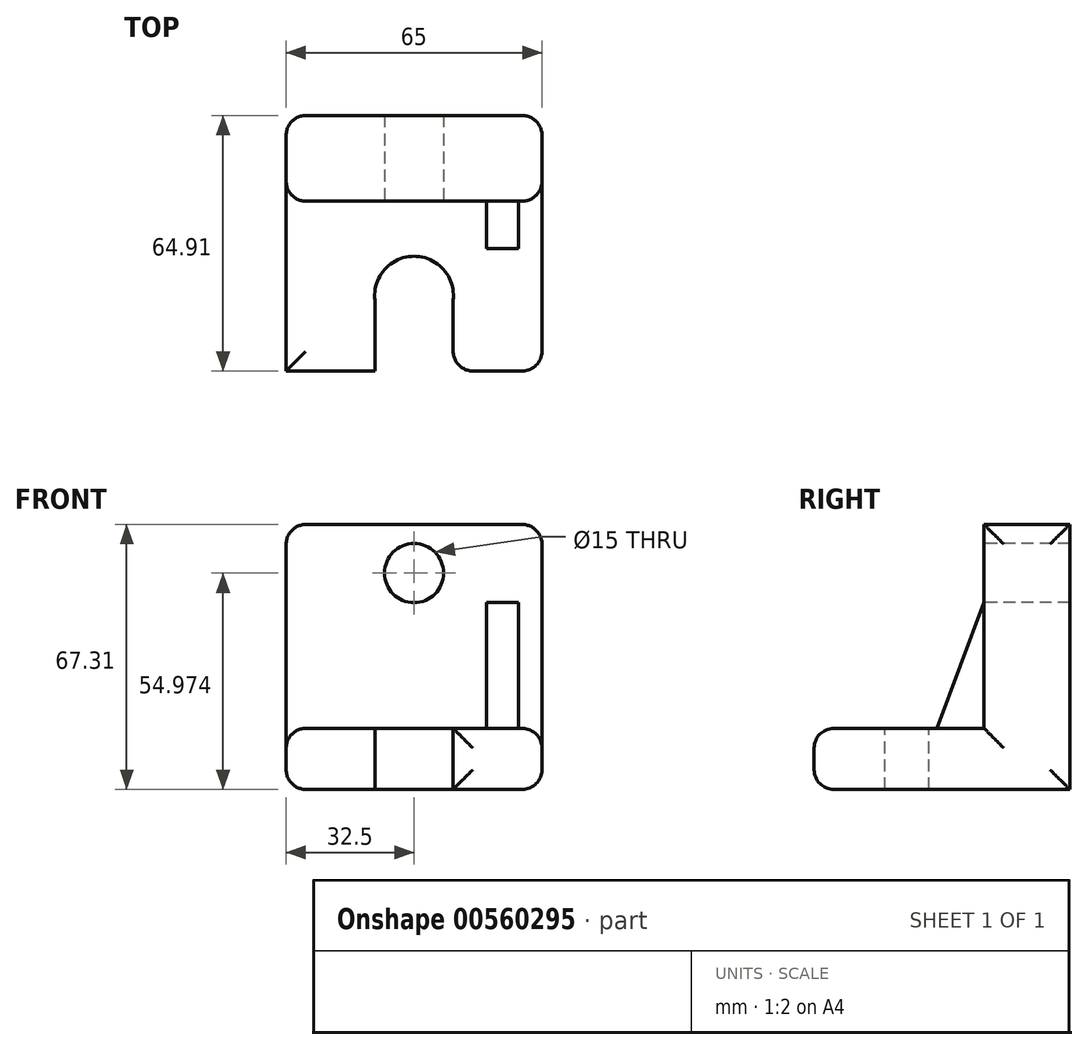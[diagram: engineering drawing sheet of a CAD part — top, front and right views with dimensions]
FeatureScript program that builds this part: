
annotation { "Feature Type Name" : "Feature", "Feature Type Description" : "" }
export const myFeature = defineFeature(function(context is Context, id is Id, definition is map)
    precondition{}
    {
        {
            var Q0;
            Q0=qCreatedBy(makeId("Right.planeOp"),FACE);
            var sketch = newSketch(context, id + "F0", { "sketchPlane" : qUnion([Q0])});
            skLineSegment(sketch, "E0", {"start": v(0, 0) * mm, "end": v(0, 67.3) * mm});
            skLineSegment(sketch, "E1", {"start": v(0, 67.3) * mm, "end": v(-21.74, 67.3) * mm});
            skLineSegment(sketch, "E2", {"start": v(-21.74, 67.3) * mm, "end": v(-21.74, 15.5) * mm});
            skLineSegment(sketch, "E3", {"start": v(-21.74, 15.5) * mm, "end": v(-64.91, 15.5) * mm});
            skLineSegment(sketch, "E4", {"start": v(-64.91, 15.5) * mm, "end": v(-64.91, 0) * mm});
            skLineSegment(sketch, "E5", {"start": v(-64.91, 0) * mm, "end": v(0, 0) * mm});
            skSolve(sketch);
        }
        {
            var Q0;
            Q0=makeQuery(id+"F0.imprint","IMPRINT",FACE,{"disambiguationData":[TD([[makeQuery(id+"F0.imprint","IMPRINT",EDGE,{"derivedFrom":sQuery(id+"F0.wireOp",EDGE,"E0")}),1.0]])]});
            extrude(context, id + "F1", {"entities" : qUnion([Q0]), "depth" : 65 * mm, "offsetDistance" : 25 * mm});
        }
        {
            var Q0;
            Q0=makeQuery(id+"F1.opExtrude","SWEPT_FACE",FACE,{"disambiguationData":[OSD([sQuery(id+"F0.wireOp",EDGE,"E2")])]});
            var sketch = newSketch(context, id + "F2", { "sketchPlane" : qUnion([Q0])});
            skCircle(sketch, "E6", {"center": v(32.5, 54.97) * mm, "radius": 7.5 * mm});
            skLineSegment(sketch, "E7", {"start": v(32.5, 67.3) * mm, "end": v(32.5, 12.95) * mm, "construction": true});
            skSolve(sketch);
        }
        {
            var Q0;
            Q0=makeQuery(id+"F2.imprint","IMPRINT",FACE,{"disambiguationData":[TD([[makeQuery(id+"F2.imprint","IMPRINT",EDGE,{"derivedFrom":sQuery(id+"F2.wireOp",EDGE,"E6")}),1.0]])]});
            extrude(context, id + "F3", {"entities" : qUnion([Q0]), "operationType" : NewBodyOperationType.REMOVE, "oppositeDirection" : true, "depth" : 25 * mm, "offsetDistance" : 25 * mm});
        }
        {
            var Q0;
            Q0=makeQuery(id+"F1.opExtrude","SWEPT_FACE",FACE,{"disambiguationData":[OSD([sQuery(id+"F0.wireOp",EDGE,"E3")])]});
            var sketch = newSketch(context, id + "F4", { "sketchPlane" : qUnion([Q0])});
            skLineSegment(sketch, "E8", {"start": v(32.5, -21.74) * mm, "end": v(32.5, -64.91) * mm, "construction": true});
            skArc(sketch, "E9", {"start": v(42.43, -46.92) * mm, "mid": v(32.5, -35.76) * mm, "end": v(22.57, -46.92) * mm});
            skLineSegment(sketch, "E10", {"start": v(22.57, -46.92) * mm, "end": v(22.57, -64.91) * mm});
            skLineSegment(sketch, "E11", {"start": v(42.43, -46.92) * mm, "end": v(42.43, -64.91) * mm});
            skSolve(sketch);
        }
        {
            var Q0;
            Q0=makeQuery(id+"F4.imprint","IMPRINT",FACE,{"disambiguationData":[TD([[makeQuery(id+"F4.imprint","IMPRINT",EDGE,{"derivedFrom":sQuery(id+"F4.wireOp",EDGE,"E9")}),1.0]])]});
            extrude(context, id + "F5", {"entities" : qUnion([Q0]), "operationType" : NewBodyOperationType.REMOVE, "endBound" : BoundingType.UP_TO_NEXT, "oppositeDirection" : true, "depth" : 10.1 * mm, "offsetDistance" : 25 * mm});
        }
        {
            var Q0;
            Q0=qCreatedBy(makeId("Right.planeOp"),FACE);
            cPlane(context, id + "F6", {"entities" : qUnion([Q0]), "cplaneType" : CPlaneType.OFFSET, "offset" : 55 * mm, "width" : 150 * mm, "height" : 150 * mm});
        }
        {
            var Q0;
            Q0=qCreatedBy(id+"F6.planeOp",FACE);
            var sketch = newSketch(context, id + "F7", { "sketchPlane" : qUnion([Q0])});
            skLineSegment(sketch, "E12.0", {"start": v(-21.74, 47.5) * mm, "end": v(-21.74, 15.5) * mm});
            skLineSegment(sketch, "E13.0", {"start": v(-21.74, 15.5) * mm, "end": v(-33.74, 15.5) * mm});
            skLineSegment(sketch, "E14.0.4", {"start": v(-21.74, 67.3) * mm, "end": v(-21.74, 15.5) * mm});
            skLineSegment(sketch, "E15", {"start": v(-21.74, 47.5) * mm, "end": v(-33.74, 15.5) * mm});
            skSolve(sketch);
        }
        {
            var Q0;
            {var subQ0=sQuery(id+"F7.wireOp",EDGE,"E13.0");Q0=makeQuery(id+"F7.imprint","IMPRINT",FACE,{"disambiguationData":[TD([[makeQuery(id+"F7.imprint","IMPRINT",EDGE,{"derivedFrom":subQ0}),-1.0]])]});}
            extrude(context, id + "F8", {"entities" : qUnion([Q0]), "operationType" : NewBodyOperationType.ADD, "endBound" : BoundingType.SYMMETRIC, "depth" : 8.2 * mm, "offsetDistance" : 25 * mm});
        }
        {
            var Q0;
            Q0=makeQuery(id+"F1.opExtrude","CAP_EDGE",EDGE,{"disambiguationData":[OSD([sQuery(id+"F0.wireOp",EDGE,"E1")])],"isStart":true});
            var Q1;
            Q1=makeQuery(id+"F1.opExtrude","CAP_EDGE",EDGE,{"disambiguationData":[OSD([sQuery(id+"F0.wireOp",EDGE,"E1")])],"isStart":false});
            var Q2;
            {var subQ0=sQuery(id+"F0.wireOp",EDGE,"E4");var subQ1=sQuery(id+"F0.wireOp",EDGE,"E3");Q2=makeQuery(id+"F5.boolean.opBoolean","SPLIT",EDGE,{"disambiguationData":[TD([makeQuery(id+"F5.opExtrude","SWEPT_FACE",FACE,{"disambiguationData":[OSD([sQuery(id+"F4.wireOp",EDGE,"E10")])]})])],"derivedFrom":makeQuery(id+"F1.opExtrude","SWEPT_EDGE",EDGE,{"disambiguationData":[OSD([subQ1,subQ0])]})});}
            var Q3;
            Q3=makeQuery(id+"F1.opExtrude","CAP_EDGE",EDGE,{"disambiguationData":[OSD([sQuery(id+"F0.wireOp",EDGE,"E3")])],"isStart":true});
            var Q4;
            Q4=makeQuery(id+"F1.opExtrude","CAP_EDGE",EDGE,{"disambiguationData":[OSD([sQuery(id+"F0.wireOp",EDGE,"E2")])],"isStart":true});
            var Q5;
            Q5=makeQuery(id+"F1.opExtrude","CAP_EDGE",EDGE,{"disambiguationData":[OSD([sQuery(id+"F0.wireOp",EDGE,"E0")])],"isStart":true});
            var Q6;
            Q6=makeQuery(id+"F1.opExtrude","CAP_EDGE",EDGE,{"disambiguationData":[OSD([sQuery(id+"F0.wireOp",EDGE,"E5")])],"isStart":true});
            var Q7;
            {var subQ0=sQuery(id+"F0.wireOp",EDGE,"E5");var subQ1=sQuery(id+"F0.wireOp",EDGE,"E4");Q7=makeQuery(id+"F5.boolean.opBoolean","SPLIT",EDGE,{"disambiguationData":[TD([makeQuery(id+"F5.opExtrude","SWEPT_FACE",FACE,{"disambiguationData":[OSD([sQuery(id+"F4.wireOp",EDGE,"E10")])]})])],"derivedFrom":makeQuery(id+"F1.opExtrude","SWEPT_EDGE",EDGE,{"disambiguationData":[OSD([subQ1,subQ0])]})});}
            var Q8;
            Q8=makeQuery(id+"F1.opExtrude","CAP_EDGE",EDGE,{"disambiguationData":[OSD([sQuery(id+"F0.wireOp",EDGE,"E4")])],"isStart":false});
            var Q9;
            Q9=makeQuery(id+"F1.opExtrude","CAP_EDGE",EDGE,{"disambiguationData":[OSD([sQuery(id+"F0.wireOp",EDGE,"E3")])],"isStart":false});
            var Q10;
            Q10=makeQuery(id+"F1.opExtrude","CAP_EDGE",EDGE,{"disambiguationData":[OSD([sQuery(id+"F0.wireOp",EDGE,"E2")])],"isStart":false});
            var Q11;
            Q11=makeQuery(id+"F1.opExtrude","CAP_EDGE",EDGE,{"disambiguationData":[OSD([sQuery(id+"F0.wireOp",EDGE,"E0")])],"isStart":false});
            var Q12;
            Q12=makeQuery(id+"F1.opExtrude","CAP_EDGE",EDGE,{"disambiguationData":[OSD([sQuery(id+"F0.wireOp",EDGE,"E5")])],"isStart":false});
            var Q13;
            {var subQ1=sQuery(id+"F0.wireOp",EDGE,"E4");Q13=makeQuery(id+"F5.boolean.opBoolean","SPLIT",FACE,{"disambiguationData":[TD([makeQuery(id+"F5.opExtrude","SWEPT_FACE",FACE,{"disambiguationData":[OSD([sQuery(id+"F4.wireOp",EDGE,"E11")])]})])],"derivedFrom":makeQuery(id+"F1.opExtrude","SWEPT_FACE",FACE,{"disambiguationData":[OSD([subQ1])]})});}
            var Q14;
            Q14=makeQuery(id+"F8.opExtrude","SWEPT_EDGE",EDGE,{"disambiguationData":[OSD([sQuery(id+"F7.wireOp",EDGE,"E13.0"),sQuery(id+"F7.wireOp",EDGE,"E15")])]});
            fillet(context, id + "F9", {"entities" : qUnion([Q0, Q1, Q2, Q3, Q4, Q5, Q6, Q7, Q8, Q9, Q10, Q11, Q12, Q13, Q14]), "radius" : 5 * mm, "tangentPropagation" : true, "allowEdgeOverflow" : false});
        }
    });
